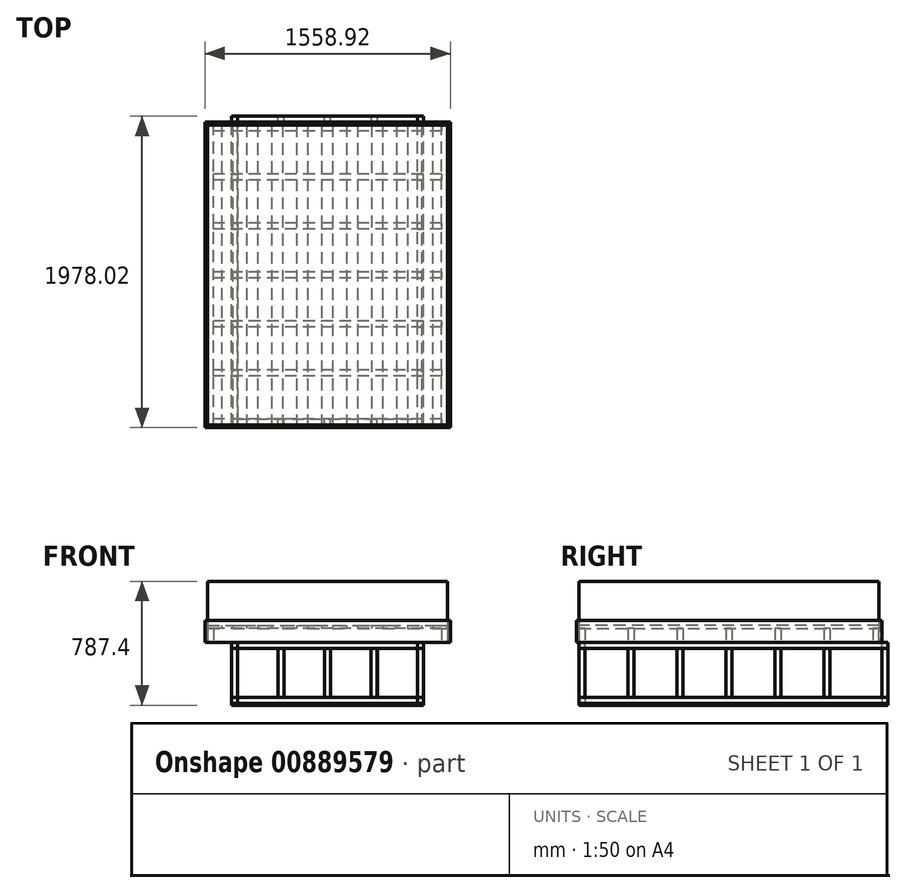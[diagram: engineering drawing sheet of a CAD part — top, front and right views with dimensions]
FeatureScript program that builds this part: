
annotation { "Feature Type Name" : "Feature", "Feature Type Description" : "" }
export const myFeature = defineFeature(function(context is Context, id is Id, definition is map)
    precondition{}
    {
        {
            var Q0;
            Q0=qCreatedBy(makeId("Top.planeOp"),FACE);
            var sketch = newSketch(context, id + "F0", { "sketchPlane" : qUnion([Q0])});
            skLineSegment(sketch, "E0.bottom", {"start": v(0, 0) * mm, "end": v(1524, 0) * mm});
            skLineSegment(sketch, "E0.top", {"start": v(0, -1905) * mm, "end": v(1524, -1905) * mm});
            skLineSegment(sketch, "E0.left", {"start": v(0, 0) * mm, "end": v(0, -1905) * mm});
            skLineSegment(sketch, "E0.right", {"start": v(1524, 0) * mm, "end": v(1524, -1905) * mm});
            skSolve(sketch);
        }
        {
            var Q0;
            Q0=makeQuery(id+"F0.imprint","IMPRINT",FACE,{"disambiguationData":[TD([[makeQuery(id+"F0.imprint","IMPRINT",EDGE,{"derivedFrom":sQuery(id+"F0.wireOp",EDGE,"E0.bottom")}),-1.0]])]});
            extrude(context, id + "F1", {"entities" : qUnion([Q0]), "depth" : 787.4 * mm, "offsetDistance" : 25.4 * mm, "hasSecondDirection" : true, "secondDirectionOppositeDirection" : true, "secondDirectionDepth" : -508 * mm});
        }
        {
            var Q0;
            Q0=makeQuery(id+"F1.opExtrude","SWEPT_FACE",FACE,{"disambiguationData":[OSD([sQuery(id+"F0.wireOp",EDGE,"E0.top")])]});
            var sketch = newSketch(context, id + "F2", { "sketchPlane" : qUnion([Q0])});
            skLineSegment(sketch, "E1.bottom", {"start": v(0, 508) * mm, "end": v(88.9, 508) * mm});
            skLineSegment(sketch, "E1.top", {"start": v(0, 488.95) * mm, "end": v(88.9, 488.95) * mm});
            skLineSegment(sketch, "E1.left", {"start": v(0, 508) * mm, "end": v(0, 488.95) * mm});
            skLineSegment(sketch, "E1.right", {"start": v(88.9, 508) * mm, "end": v(88.9, 488.95) * mm});
            skLineSegment(sketch, "E2.1.0.0", {"start": v(158.75, 508) * mm, "end": v(247.65, 508) * mm});
            skLineSegment(sketch, "E2.1.0.1", {"start": v(158.75, 508) * mm, "end": v(158.75, 488.95) * mm});
            skLineSegment(sketch, "E2.1.0.2", {"start": v(158.75, 488.95) * mm, "end": v(247.65, 488.95) * mm});
            skLineSegment(sketch, "E2.1.0.3", {"start": v(247.65, 508) * mm, "end": v(247.65, 488.95) * mm});
            skLineSegment(sketch, "E2.2.0.0", {"start": v(317.5, 508) * mm, "end": v(406.4, 508) * mm});
            skLineSegment(sketch, "E2.2.0.1", {"start": v(317.5, 508) * mm, "end": v(317.5, 488.95) * mm});
            skLineSegment(sketch, "E2.2.0.2", {"start": v(317.5, 488.95) * mm, "end": v(406.4, 488.95) * mm});
            skLineSegment(sketch, "E2.2.0.3", {"start": v(406.4, 508) * mm, "end": v(406.4, 488.95) * mm});
            skLineSegment(sketch, "E2.3.0.0", {"start": v(476.25, 508) * mm, "end": v(565.15, 508) * mm});
            skLineSegment(sketch, "E2.3.0.1", {"start": v(476.25, 508) * mm, "end": v(476.25, 488.95) * mm});
            skLineSegment(sketch, "E2.3.0.2", {"start": v(476.25, 488.95) * mm, "end": v(565.15, 488.95) * mm});
            skLineSegment(sketch, "E2.3.0.3", {"start": v(565.15, 508) * mm, "end": v(565.15, 488.95) * mm});
            skLineSegment(sketch, "E2.4.0.0", {"start": v(635, 508) * mm, "end": v(723.9, 508) * mm});
            skLineSegment(sketch, "E2.4.0.1", {"start": v(635, 508) * mm, "end": v(635, 488.95) * mm});
            skLineSegment(sketch, "E2.4.0.2", {"start": v(635, 488.95) * mm, "end": v(723.9, 488.95) * mm});
            skLineSegment(sketch, "E2.4.0.3", {"start": v(723.9, 508) * mm, "end": v(723.9, 488.95) * mm});
            skLineSegment(sketch, "E2.5.0.0", {"start": v(793.75, 508) * mm, "end": v(882.65, 508) * mm});
            skLineSegment(sketch, "E2.5.0.1", {"start": v(793.75, 508) * mm, "end": v(793.75, 488.95) * mm});
            skLineSegment(sketch, "E2.5.0.2", {"start": v(793.75, 488.95) * mm, "end": v(882.65, 488.95) * mm});
            skLineSegment(sketch, "E2.5.0.3", {"start": v(882.65, 508) * mm, "end": v(882.65, 488.95) * mm});
            skLineSegment(sketch, "E2.6.0.0", {"start": v(952.5, 508) * mm, "end": v(1041.4, 508) * mm});
            skLineSegment(sketch, "E2.6.0.1", {"start": v(952.5, 508) * mm, "end": v(952.5, 488.95) * mm});
            skLineSegment(sketch, "E2.6.0.2", {"start": v(952.5, 488.95) * mm, "end": v(1041.4, 488.95) * mm});
            skLineSegment(sketch, "E2.6.0.3", {"start": v(1041.4, 508) * mm, "end": v(1041.4, 488.95) * mm});
            skLineSegment(sketch, "E2.7.0.0", {"start": v(1111.25, 508) * mm, "end": v(1200.15, 508) * mm});
            skLineSegment(sketch, "E2.7.0.1", {"start": v(1111.25, 508) * mm, "end": v(1111.25, 488.95) * mm});
            skLineSegment(sketch, "E2.7.0.2", {"start": v(1111.25, 488.95) * mm, "end": v(1200.15, 488.95) * mm});
            skLineSegment(sketch, "E2.7.0.3", {"start": v(1200.15, 508) * mm, "end": v(1200.15, 488.95) * mm});
            skLineSegment(sketch, "E2.8.0.0", {"start": v(1270, 508) * mm, "end": v(1358.9, 508) * mm});
            skLineSegment(sketch, "E2.8.0.1", {"start": v(1270, 508) * mm, "end": v(1270, 488.95) * mm});
            skLineSegment(sketch, "E2.8.0.2", {"start": v(1270, 488.95) * mm, "end": v(1358.9, 488.95) * mm});
            skLineSegment(sketch, "E2.8.0.3", {"start": v(1358.9, 508) * mm, "end": v(1358.9, 488.95) * mm});
            skLineSegment(sketch, "E2.9.0.0", {"start": v(1428.75, 508) * mm, "end": v(1517.65, 508) * mm});
            skLineSegment(sketch, "E2.9.0.1", {"start": v(1428.75, 508) * mm, "end": v(1428.75, 488.95) * mm});
            skLineSegment(sketch, "E2.9.0.2", {"start": v(1428.75, 488.95) * mm, "end": v(1517.65, 488.95) * mm});
            skLineSegment(sketch, "E2.9.0.3", {"start": v(1517.65, 508) * mm, "end": v(1517.65, 488.95) * mm});
            skLineSegment(sketch, "E2.direction1", {"start": v(0, 508) * mm, "end": v(158.75, 508) * mm, "construction": true});
            skSolve(sketch);
        }
        {
            var Q0;
            Q0 = qSketchRegion(id + "F2", true);
            var Q1;
            Q1=makeQuery(id+"F1.opExtrude","SWEPT_FACE",FACE,{"disambiguationData":[OSD([sQuery(id+"F0.wireOp",EDGE,"E0.bottom")])]});
            extrude(context, id + "F3", {"entities" : qUnion([Q0]), "endBound" : BoundingType.UP_TO_SURFACE, "oppositeDirection" : true, "depth" : 25.4 * mm, "endBoundEntityFace" : qUnion([Q1]), "offsetDistance" : 25.4 * mm});
        }
        {
            var Q0;
            Q0=makeQuery(id+"F1.opExtrude","SWEPT_FACE",FACE,{"disambiguationData":[OSD([sQuery(id+"F0.wireOp",EDGE,"E0.bottom")])]});
            var sketch = newSketch(context, id + "F4", { "sketchPlane" : qUnion([Q0])});
            skLineSegment(sketch, "E3.bottom", {"start": v(-1524, 400.05) * mm, "end": v(-1485.9, 400.05) * mm});
            skLineSegment(sketch, "E3.top", {"start": v(-1524, 488.95) * mm, "end": v(-1485.9, 488.95) * mm});
            skLineSegment(sketch, "E3.left", {"start": v(-1524, 400.05) * mm, "end": v(-1524, 488.95) * mm});
            skLineSegment(sketch, "E3.right", {"start": v(-1485.9, 400.05) * mm, "end": v(-1485.9, 488.95) * mm});
            skLineSegment(sketch, "E4.bottom", {"start": v(0, 400.05) * mm, "end": v(-38.1, 400.05) * mm});
            skLineSegment(sketch, "E4.top", {"start": v(0, 488.95) * mm, "end": v(-38.1, 488.95) * mm});
            skLineSegment(sketch, "E4.left", {"start": v(0, 400.05) * mm, "end": v(0, 488.95) * mm});
            skLineSegment(sketch, "E4.right", {"start": v(-38.1, 400.05) * mm, "end": v(-38.1, 488.95) * mm});
            skSolve(sketch);
        }
        {
            var Q0;
            Q0 = qSketchRegion(id + "F4", true);
            var Q1;
            Q1=makeQuery(id+"F1.opExtrude","SWEPT_FACE",FACE,{"disambiguationData":[OSD([sQuery(id+"F0.wireOp",EDGE,"E0.top")])]});
            extrude(context, id + "F5", {"entities" : qUnion([Q0]), "endBound" : BoundingType.UP_TO_SURFACE, "oppositeDirection" : true, "depth" : 25.4 * mm, "endBoundEntityFace" : qUnion([Q1]), "offsetDistance" : 25.4 * mm});
        }
        {
            var Q0;
            Q0=makeQuery(id+"F5.opExtrude","SWEPT_FACE",FACE,{"disambiguationData":[OSD([sQuery(id+"F4.wireOp",EDGE,"E4.right")])]});
            var sketch = newSketch(context, id + "F6", { "sketchPlane" : qUnion([Q0])});
            skLineSegment(sketch, "E5.bottom", {"start": v(0, 400.05) * mm, "end": v(-38.1, 400.05) * mm});
            skLineSegment(sketch, "E5.top", {"start": v(0, 488.95) * mm, "end": v(-38.1, 488.95) * mm});
            skLineSegment(sketch, "E5.left", {"start": v(0, 400.05) * mm, "end": v(0, 488.95) * mm});
            skLineSegment(sketch, "E5.right", {"start": v(-38.1, 400.05) * mm, "end": v(-38.1, 488.95) * mm});
            skLineSegment(sketch, "E6.1.0.0", {"start": v(-311.15, 400.05) * mm, "end": v(-349.25, 400.05) * mm});
            skLineSegment(sketch, "E6.1.0.1", {"start": v(-311.15, 488.95) * mm, "end": v(-349.25, 488.95) * mm});
            skLineSegment(sketch, "E6.1.0.2", {"start": v(-311.15, 400.05) * mm, "end": v(-311.15, 488.95) * mm});
            skLineSegment(sketch, "E6.1.0.3", {"start": v(-349.25, 400.05) * mm, "end": v(-349.25, 488.95) * mm});
            skLineSegment(sketch, "E6.2.0.0", {"start": v(-622.3, 400.05) * mm, "end": v(-660.4, 400.05) * mm});
            skLineSegment(sketch, "E6.2.0.1", {"start": v(-622.3, 488.95) * mm, "end": v(-660.4, 488.95) * mm});
            skLineSegment(sketch, "E6.2.0.2", {"start": v(-622.3, 400.05) * mm, "end": v(-622.3, 488.95) * mm});
            skLineSegment(sketch, "E6.2.0.3", {"start": v(-660.4, 400.05) * mm, "end": v(-660.4, 488.95) * mm});
            skLineSegment(sketch, "E6.3.0.0", {"start": v(-933.45, 400.05) * mm, "end": v(-971.55, 400.05) * mm});
            skLineSegment(sketch, "E6.3.0.1", {"start": v(-933.45, 488.95) * mm, "end": v(-971.55, 488.95) * mm});
            skLineSegment(sketch, "E6.3.0.2", {"start": v(-933.45, 400.05) * mm, "end": v(-933.45, 488.95) * mm});
            skLineSegment(sketch, "E6.3.0.3", {"start": v(-971.55, 400.05) * mm, "end": v(-971.55, 488.95) * mm});
            skLineSegment(sketch, "E6.4.0.0", {"start": v(-1244.6, 400.05) * mm, "end": v(-1282.7, 400.05) * mm});
            skLineSegment(sketch, "E6.4.0.1", {"start": v(-1244.6, 488.95) * mm, "end": v(-1282.7, 488.95) * mm});
            skLineSegment(sketch, "E6.4.0.2", {"start": v(-1244.6, 400.05) * mm, "end": v(-1244.6, 488.95) * mm});
            skLineSegment(sketch, "E6.4.0.3", {"start": v(-1282.7, 400.05) * mm, "end": v(-1282.7, 488.95) * mm});
            skLineSegment(sketch, "E6.5.0.0", {"start": v(-1555.75, 400.05) * mm, "end": v(-1593.85, 400.05) * mm});
            skLineSegment(sketch, "E6.5.0.1", {"start": v(-1555.75, 488.95) * mm, "end": v(-1593.85, 488.95) * mm});
            skLineSegment(sketch, "E6.5.0.2", {"start": v(-1555.75, 400.05) * mm, "end": v(-1555.75, 488.95) * mm});
            skLineSegment(sketch, "E6.5.0.3", {"start": v(-1593.85, 400.05) * mm, "end": v(-1593.85, 488.95) * mm});
            skLineSegment(sketch, "E6.6.0.0", {"start": v(-1866.9, 400.05) * mm, "end": v(-1905, 400.05) * mm});
            skLineSegment(sketch, "E6.6.0.1", {"start": v(-1866.9, 488.95) * mm, "end": v(-1905, 488.95) * mm});
            skLineSegment(sketch, "E6.6.0.2", {"start": v(-1866.9, 400.05) * mm, "end": v(-1866.9, 488.95) * mm});
            skLineSegment(sketch, "E6.6.0.3", {"start": v(-1905, 400.05) * mm, "end": v(-1905, 488.95) * mm});
            skLineSegment(sketch, "E6.direction1", {"start": v(-38.1, 400.05) * mm, "end": v(-349.25, 400.05) * mm, "construction": true});
            skSolve(sketch);
        }
        {
            var Q0;
            Q0 = qSketchRegion(id + "F6", true);
            var Q1;
            Q1=makeQuery(id+"F5.opExtrude","SWEPT_FACE",FACE,{"disambiguationData":[OSD([sQuery(id+"F4.wireOp",EDGE,"E3.right")])]});
            extrude(context, id + "F7", {"entities" : qUnion([Q0]), "endBound" : BoundingType.UP_TO_SURFACE, "depth" : 25.4 * mm, "endBoundEntityFace" : qUnion([Q1]), "offsetDistance" : 25.4 * mm});
        }
        {
            var Q0;
            Q0=makeQuery(id+"F5.opExtrude","SWEPT_FACE",FACE,{"disambiguationData":[OSD([sQuery(id+"F4.wireOp",EDGE,"E4.bottom")])]});
            var sketch = newSketch(context, id + "F8", { "sketchPlane" : qUnion([Q0])});
            skLineSegment(sketch, "E7.left", {"start": v(1541.46, -17.46) * mm, "end": v(1541.46, 1922.46) * mm});
            skLineSegment(sketch, "E7.right", {"start": v(-17.46, -17.46) * mm, "end": v(-17.46, 1922.46) * mm});
            skLineSegment(sketch, "E8.left", {"start": v(1524, 0) * mm, "end": v(1524, 1905) * mm});
            skLineSegment(sketch, "E8.right", {"start": v(0, 0) * mm, "end": v(0, 1905) * mm});
            skLineSegment(sketch, "E9", {"start": v(0, 1905) * mm, "end": v(-17.46, 1922.46) * mm});
            skLineSegment(sketch, "E10", {"start": v(1524, 1905) * mm, "end": v(1541.46, 1922.46) * mm});
            skLineSegment(sketch, "E11", {"start": v(1524, 0) * mm, "end": v(1541.46, -17.46) * mm});
            skLineSegment(sketch, "E12", {"start": v(0, 0) * mm, "end": v(-17.46, -17.46) * mm});
            skSolve(sketch);
        }
        {
            var Q0;
            Q0=makeQuery(id+"F7.opExtrude","SWEPT_FACE",FACE,{"disambiguationData":[OSD([sQuery(id+"F6.wireOp",EDGE,"E5.bottom")])]});
            var sketch = newSketch(context, id + "F9", { "sketchPlane" : qUnion([Q0])});
            skLineSegment(sketch, "E13.0", {"start": v(1524, 0) * mm, "end": v(1541.46, -17.46) * mm});
            skLineSegment(sketch, "E14.0", {"start": v(0, 0) * mm, "end": v(-17.46, -17.46) * mm});
            skLineSegment(sketch, "E15", {"start": v(0, 0) * mm, "end": v(1524, 0) * mm});
            skLineSegment(sketch, "E16", {"start": v(1541.46, -17.46) * mm, "end": v(-17.46, -17.46) * mm});
            skLineSegment(sketch, "E17.0", {"start": v(0, 1905) * mm, "end": v(-17.46, 1922.46) * mm});
            skLineSegment(sketch, "E18.0", {"start": v(1524, 1905) * mm, "end": v(1541.46, 1922.46) * mm});
            skLineSegment(sketch, "E19", {"start": v(1524, 1905) * mm, "end": v(0, 1905) * mm});
            skLineSegment(sketch, "E20", {"start": v(-17.46, 1922.46) * mm, "end": v(1541.46, 1922.46) * mm});
            skSolve(sketch);
        }
        {
            var Q0;
            Q0 = qSketchRegion(id + "F8", true);
            var Q1;
            Q1 = qSketchRegion(id + "F9", true);
            extrude(context, id + "F10", {"entities" : qUnion([Q0, Q1]), "oppositeDirection" : true, "depth" : 139.7 * mm, "offsetDistance" : 25.4 * mm});
        }
        {
            var Q0;
            Q0=makeQuery(id+"F7.opExtrude","SWEPT_FACE",FACE,{"disambiguationData":[OSD([sQuery(id+"F6.wireOp",EDGE,"E6.5.0.0")])]});
            var sketch = newSketch(context, id + "F11", { "sketchPlane" : qUnion([Q0])});
            skLineSegment(sketch, "E21.bottom", {"start": v(152.41, 1905) * mm, "end": v(190.51, 1905) * mm});
            skLineSegment(sketch, "E21.top", {"start": v(152.41, -55.56) * mm, "end": v(190.51, -55.56) * mm});
            skLineSegment(sketch, "E21.left", {"start": v(152.41, 1905) * mm, "end": v(152.41, -55.56) * mm});
            skLineSegment(sketch, "E21.right", {"start": v(190.51, 1905) * mm, "end": v(190.51, -55.56) * mm});
            skLineSegment(sketch, "E22.bottom", {"start": v(1333.49, 1905) * mm, "end": v(1371.59, 1905) * mm});
            skLineSegment(sketch, "E22.top", {"start": v(1333.49, -55.56) * mm, "end": v(1371.59, -55.56) * mm});
            skLineSegment(sketch, "E22.left", {"start": v(1333.49, 1905) * mm, "end": v(1333.49, -55.56) * mm});
            skLineSegment(sketch, "E22.right", {"start": v(1371.59, 1905) * mm, "end": v(1371.59, -55.56) * mm});
            skSolve(sketch);
        }
        {
            var Q0;
            Q0=makeQuery(id+"F7.opExtrude","SWEPT_FACE",FACE,{"disambiguationData":[OSD([sQuery(id+"F6.wireOp",EDGE,"E6.1.0.0")])]});
            var sketch = newSketch(context, id + "F12", { "sketchPlane" : qUnion([Q0])});
            skLineSegment(sketch, "E23.bottom", {"start": v(190.51, 1905) * mm, "end": v(1333.49, 1905) * mm});
            skLineSegment(sketch, "E23.top", {"start": v(190.51, 1866.9) * mm, "end": v(1333.49, 1866.9) * mm});
            skLineSegment(sketch, "E23.left", {"start": v(190.51, 1905) * mm, "end": v(190.51, 1866.9) * mm});
            skLineSegment(sketch, "E23.right", {"start": v(1333.49, 1905) * mm, "end": v(1333.49, 1866.9) * mm});
            skLineSegment(sketch, "E24.bottom", {"start": v(190.51, -17.46) * mm, "end": v(1333.49, -17.46) * mm});
            skLineSegment(sketch, "E24.top", {"start": v(190.51, -55.56) * mm, "end": v(1333.49, -55.56) * mm});
            skLineSegment(sketch, "E24.left", {"start": v(190.51, -17.46) * mm, "end": v(190.51, -55.56) * mm});
            skLineSegment(sketch, "E24.right", {"start": v(1333.49, -17.46) * mm, "end": v(1333.49, -55.56) * mm});
            skSolve(sketch);
        }
        {
            var Q0;
            Q0 = qSketchRegion(id + "F11", true);
            var Q1;
            Q1 = qSketchRegion(id + "F12", true);
            extrude(context, id + "F13", {"entities" : qUnion([Q0, Q1]), "depth" : 38.1 * mm, "offsetDistance" : 25.4 * mm});
        }
        {
            var Q0;
            Q0=qCreatedBy(makeId("Top.planeOp"),FACE);
            var sketch = newSketch(context, id + "F14", { "sketchPlane" : qUnion([Q0])});
            skLineSegment(sketch, "E25.0", {"start": v(152.41, -1905) * mm, "end": v(152.41, 55.56) * mm});
            skLineSegment(sketch, "E26.0", {"start": v(152.41, 55.56) * mm, "end": v(1371.59, 55.56) * mm});
            skLineSegment(sketch, "E27.0", {"start": v(152.41, -1905) * mm, "end": v(1371.59, -1905) * mm});
            skLineSegment(sketch, "E28.0", {"start": v(1371.59, -1905) * mm, "end": v(1371.59, 55.56) * mm});
            skPoint(sketch, "E29.orphan", {"position": v(1333.49, 55.56) * mm});
            skPoint(sketch, "E30.orphan", {"position": v(1333.49, -1905) * mm});
            skPoint(sketch, "E31.orphan", {"position": v(190.51, -1905) * mm});
            skPoint(sketch, "E32.orphan", {"position": v(190.51, 55.56) * mm});
            skSolve(sketch);
        }
        {
            var Q0;
            Q0 = qSketchRegion(id + "F14", true);
            extrude(context, id + "F15", {"entities" : qUnion([Q0]), "depth" : 12.7 * mm, "offsetDistance" : 25.4 * mm});
        }
        {
            var Q0;
            Q0=makeQuery(id+"F15.opExtrude","CAP_FACE",FACE,{"disambiguationData":[OSD([sQuery(id+"F14.wireOp",EDGE,"E25.0"),sQuery(id+"F14.wireOp",EDGE,"E26.0"),sQuery(id+"F14.wireOp",EDGE,"E27.0"),sQuery(id+"F14.wireOp",EDGE,"E28.0")])],"isStart":false});
            var sketch = newSketch(context, id + "F16", { "sketchPlane" : qUnion([Q0])});
            skLineSegment(sketch, "E33.0.0", {"start": v(1371.59, 55.56) * mm, "end": v(1371.59, -1905) * mm});
            skLineSegment(sketch, "E33.0.1", {"start": v(1371.59, -1905) * mm, "end": v(1333.49, -1905) * mm});
            skLineSegment(sketch, "E33.0.2", {"start": v(1333.49, -1905) * mm, "end": v(1333.49, 55.56) * mm});
            skLineSegment(sketch, "E33.0.3", {"start": v(1333.49, 55.56) * mm, "end": v(1371.59, 55.56) * mm});
            skLineSegment(sketch, "E34.0.0", {"start": v(152.41, 55.56) * mm, "end": v(190.51, 55.56) * mm});
            skLineSegment(sketch, "E34.0.1", {"start": v(190.51, 55.56) * mm, "end": v(190.51, -1905) * mm});
            skLineSegment(sketch, "E34.0.2", {"start": v(190.51, -1905) * mm, "end": v(152.41, -1905) * mm});
            skLineSegment(sketch, "E34.0.3", {"start": v(152.41, -1905) * mm, "end": v(152.41, 55.56) * mm});
            skSolve(sketch);
        }
        {
            var Q0;
            {var subQ0=sQuery(id+"F16.wireOp",EDGE,"E33.0.2");Q0=makeQuery(id+"F16.imprint","IMPRINT",FACE,{"disambiguationData":[TD([[makeQuery(id+"F16.imprint","IMPRINT",EDGE,{"derivedFrom":subQ0}),1.0]])]});}
            var sketch = newSketch(context, id + "F17", { "sketchPlane" : qUnion([Q0])});
            skLineSegment(sketch, "E35.0.0", {"start": v(190.51, -1905) * mm, "end": v(190.51, -1866.9) * mm});
            skLineSegment(sketch, "E35.0.1", {"start": v(190.51, -1866.9) * mm, "end": v(1333.49, -1866.9) * mm});
            skLineSegment(sketch, "E35.0.2", {"start": v(1333.49, -1866.9) * mm, "end": v(1333.49, -1905) * mm});
            skLineSegment(sketch, "E35.0.3", {"start": v(1333.49, -1905) * mm, "end": v(190.51, -1905) * mm});
            skLineSegment(sketch, "E36.0.0", {"start": v(190.51, 17.46) * mm, "end": v(190.51, 55.56) * mm});
            skLineSegment(sketch, "E36.0.1", {"start": v(190.51, 55.56) * mm, "end": v(1333.49, 55.56) * mm});
            skLineSegment(sketch, "E36.0.2", {"start": v(1333.49, 55.56) * mm, "end": v(1333.49, 17.46) * mm});
            skLineSegment(sketch, "E36.0.3", {"start": v(1333.49, 17.46) * mm, "end": v(190.51, 17.46) * mm});
            skSolve(sketch);
        }
        {
            var Q0;
            Q0 = qSketchRegion(id + "F16", true);
            var Q1;
            Q1 = qSketchRegion(id + "F17", true);
            extrude(context, id + "F18", {"entities" : qUnion([Q0, Q1]), "depth" : 38.1 * mm, "offsetDistance" : 25.4 * mm});
        }
        {
            var Q0;
            Q0=makeQuery(id+"F13.opExtrude","CAP_FACE",FACE,{"disambiguationData":[OSD([sQuery(id+"F11.wireOp",EDGE,"E21.bottom"),sQuery(id+"F11.wireOp",EDGE,"E21.top"),sQuery(id+"F11.wireOp",EDGE,"E21.left"),sQuery(id+"F11.wireOp",EDGE,"E21.right")])],"isStart":false});
            var sketch = newSketch(context, id + "F19", { "sketchPlane" : qUnion([Q0])});
            skLineSegment(sketch, "E37.bottom", {"start": v(152.41, 1866.9) * mm, "end": v(190.51, 1866.9) * mm});
            skLineSegment(sketch, "E37.top", {"start": v(152.41, 1905) * mm, "end": v(190.51, 1905) * mm});
            skLineSegment(sketch, "E37.left", {"start": v(152.41, 1866.9) * mm, "end": v(152.41, 1905) * mm});
            skLineSegment(sketch, "E37.right", {"start": v(190.51, 1866.9) * mm, "end": v(190.51, 1905) * mm});
            skLineSegment(sketch, "E38.bottom", {"start": v(190.51, 1555.75) * mm, "end": v(152.41, 1555.75) * mm});
            skLineSegment(sketch, "E38.top", {"start": v(190.51, 1593.85) * mm, "end": v(152.41, 1593.85) * mm});
            skLineSegment(sketch, "E38.left", {"start": v(190.51, 1555.75) * mm, "end": v(190.51, 1593.85) * mm});
            skLineSegment(sketch, "E38.right", {"start": v(152.41, 1555.75) * mm, "end": v(152.41, 1593.85) * mm});
            skLineSegment(sketch, "E39.0.1.0", {"start": v(190.51, 1244.6) * mm, "end": v(152.41, 1244.6) * mm});
            skLineSegment(sketch, "E39.0.1.1", {"start": v(190.51, 1244.6) * mm, "end": v(190.51, 1282.7) * mm});
            skLineSegment(sketch, "E39.0.1.2", {"start": v(190.51, 1282.7) * mm, "end": v(152.41, 1282.7) * mm});
            skLineSegment(sketch, "E39.0.1.3", {"start": v(152.41, 1244.6) * mm, "end": v(152.41, 1282.7) * mm});
            skLineSegment(sketch, "E39.0.2.0", {"start": v(190.51, 933.45) * mm, "end": v(152.41, 933.45) * mm});
            skLineSegment(sketch, "E39.0.2.1", {"start": v(190.51, 933.45) * mm, "end": v(190.51, 971.55) * mm});
            skLineSegment(sketch, "E39.0.2.2", {"start": v(190.51, 971.55) * mm, "end": v(152.41, 971.55) * mm});
            skLineSegment(sketch, "E39.0.2.3", {"start": v(152.41, 933.45) * mm, "end": v(152.41, 971.55) * mm});
            skLineSegment(sketch, "E39.0.3.0", {"start": v(190.51, 622.3) * mm, "end": v(152.41, 622.3) * mm});
            skLineSegment(sketch, "E39.0.3.1", {"start": v(190.51, 622.3) * mm, "end": v(190.51, 660.4) * mm});
            skLineSegment(sketch, "E39.0.3.2", {"start": v(190.51, 660.4) * mm, "end": v(152.41, 660.4) * mm});
            skLineSegment(sketch, "E39.0.3.3", {"start": v(152.41, 622.3) * mm, "end": v(152.41, 660.4) * mm});
            skLineSegment(sketch, "E39.0.4.0", {"start": v(190.51, 311.15) * mm, "end": v(152.41, 311.15) * mm});
            skLineSegment(sketch, "E39.0.4.1", {"start": v(190.51, 311.15) * mm, "end": v(190.51, 349.25) * mm});
            skLineSegment(sketch, "E39.0.4.2", {"start": v(190.51, 349.25) * mm, "end": v(152.41, 349.25) * mm});
            skLineSegment(sketch, "E39.0.4.3", {"start": v(152.41, 311.15) * mm, "end": v(152.41, 349.25) * mm});
            skLineSegment(sketch, "E39.1.0.0", {"start": v(1371.61, 1555.75) * mm, "end": v(1333.51, 1555.75) * mm});
            skLineSegment(sketch, "E39.1.0.1", {"start": v(1371.61, 1555.75) * mm, "end": v(1371.61, 1593.85) * mm});
            skLineSegment(sketch, "E39.1.0.2", {"start": v(1371.61, 1593.85) * mm, "end": v(1333.51, 1593.85) * mm});
            skLineSegment(sketch, "E39.1.0.3", {"start": v(1333.51, 1555.75) * mm, "end": v(1333.51, 1593.85) * mm});
            skLineSegment(sketch, "E39.1.1.0", {"start": v(1371.61, 1244.6) * mm, "end": v(1333.51, 1244.6) * mm});
            skLineSegment(sketch, "E39.1.1.1", {"start": v(1371.61, 1244.6) * mm, "end": v(1371.61, 1282.7) * mm});
            skLineSegment(sketch, "E39.1.1.2", {"start": v(1371.61, 1282.7) * mm, "end": v(1333.51, 1282.7) * mm});
            skLineSegment(sketch, "E39.1.1.3", {"start": v(1333.51, 1244.6) * mm, "end": v(1333.51, 1282.7) * mm});
            skLineSegment(sketch, "E39.1.2.0", {"start": v(1371.61, 933.45) * mm, "end": v(1333.51, 933.45) * mm});
            skLineSegment(sketch, "E39.1.2.1", {"start": v(1371.61, 933.45) * mm, "end": v(1371.61, 971.55) * mm});
            skLineSegment(sketch, "E39.1.2.2", {"start": v(1371.61, 971.55) * mm, "end": v(1333.51, 971.55) * mm});
            skLineSegment(sketch, "E39.1.2.3", {"start": v(1333.51, 933.45) * mm, "end": v(1333.51, 971.55) * mm});
            skLineSegment(sketch, "E39.1.3.0", {"start": v(1371.61, 622.3) * mm, "end": v(1333.51, 622.3) * mm});
            skLineSegment(sketch, "E39.1.3.1", {"start": v(1371.61, 622.3) * mm, "end": v(1371.61, 660.4) * mm});
            skLineSegment(sketch, "E39.1.3.2", {"start": v(1371.61, 660.4) * mm, "end": v(1333.51, 660.4) * mm});
            skLineSegment(sketch, "E39.1.3.3", {"start": v(1333.51, 622.3) * mm, "end": v(1333.51, 660.4) * mm});
            skLineSegment(sketch, "E39.1.4.0", {"start": v(1371.61, 311.15) * mm, "end": v(1333.51, 311.15) * mm});
            skLineSegment(sketch, "E39.1.4.1", {"start": v(1371.61, 311.15) * mm, "end": v(1371.61, 349.25) * mm});
            skLineSegment(sketch, "E39.1.4.2", {"start": v(1371.61, 349.25) * mm, "end": v(1333.51, 349.25) * mm});
            skLineSegment(sketch, "E39.1.4.3", {"start": v(1333.51, 311.15) * mm, "end": v(1333.51, 349.25) * mm});
            skLineSegment(sketch, "E39.direction1", {"start": v(152.41, 1555.75) * mm, "end": v(1333.51, 1555.75) * mm, "construction": true});
            skLineSegment(sketch, "E39.direction2", {"start": v(152.41, 1555.75) * mm, "end": v(152.41, 1244.6) * mm, "construction": true});
            skLineSegment(sketch, "E40.1.0.0", {"start": v(447.69, 1866.9) * mm, "end": v(485.79, 1866.9) * mm});
            skLineSegment(sketch, "E40.1.0.1", {"start": v(447.69, 1866.9) * mm, "end": v(447.69, 1905) * mm});
            skLineSegment(sketch, "E40.1.0.2", {"start": v(447.69, 1905) * mm, "end": v(485.79, 1905) * mm});
            skLineSegment(sketch, "E40.1.0.3", {"start": v(485.79, 1866.9) * mm, "end": v(485.79, 1905) * mm});
            skLineSegment(sketch, "E40.2.0.0", {"start": v(742.96, 1866.9) * mm, "end": v(781.06, 1866.9) * mm});
            skLineSegment(sketch, "E40.2.0.1", {"start": v(742.96, 1866.9) * mm, "end": v(742.96, 1905) * mm});
            skLineSegment(sketch, "E40.2.0.2", {"start": v(742.96, 1905) * mm, "end": v(781.06, 1905) * mm});
            skLineSegment(sketch, "E40.2.0.3", {"start": v(781.06, 1866.9) * mm, "end": v(781.06, 1905) * mm});
            skLineSegment(sketch, "E40.3.0.0", {"start": v(1038.24, 1866.9) * mm, "end": v(1076.34, 1866.9) * mm});
            skLineSegment(sketch, "E40.3.0.1", {"start": v(1038.24, 1866.9) * mm, "end": v(1038.24, 1905) * mm});
            skLineSegment(sketch, "E40.3.0.2", {"start": v(1038.24, 1905) * mm, "end": v(1076.34, 1905) * mm});
            skLineSegment(sketch, "E40.3.0.3", {"start": v(1076.34, 1866.9) * mm, "end": v(1076.34, 1905) * mm});
            skLineSegment(sketch, "E40.4.0.0", {"start": v(1333.51, 1866.9) * mm, "end": v(1371.61, 1866.9) * mm});
            skLineSegment(sketch, "E40.4.0.1", {"start": v(1333.51, 1866.9) * mm, "end": v(1333.51, 1905) * mm});
            skLineSegment(sketch, "E40.4.0.2", {"start": v(1333.51, 1905) * mm, "end": v(1371.61, 1905) * mm});
            skLineSegment(sketch, "E40.4.0.3", {"start": v(1371.61, 1866.9) * mm, "end": v(1371.61, 1905) * mm});
            skLineSegment(sketch, "E40.direction1", {"start": v(152.41, 1866.9) * mm, "end": v(447.69, 1866.9) * mm, "construction": true});
            skLineSegment(sketch, "E41.1.4.0", {"start": v(1371.59, -55.56) * mm, "end": v(1333.49, -55.56) * mm});
            skLineSegment(sketch, "E41.1.4.1", {"start": v(1371.59, -55.56) * mm, "end": v(1371.59, -17.46) * mm});
            skLineSegment(sketch, "E41.1.4.2", {"start": v(1371.59, -17.46) * mm, "end": v(1333.49, -17.46) * mm});
            skLineSegment(sketch, "E41.1.4.3", {"start": v(1333.49, -55.56) * mm, "end": v(1333.49, -17.46) * mm});
            skLineSegment(sketch, "E42.1.1.0", {"start": v(152.41, -55.56) * mm, "end": v(190.51, -55.56) * mm});
            skLineSegment(sketch, "E42.1.1.1", {"start": v(152.41, -55.56) * mm, "end": v(152.41, -17.46) * mm});
            skLineSegment(sketch, "E42.1.1.2", {"start": v(152.41, -17.46) * mm, "end": v(190.51, -17.46) * mm});
            skLineSegment(sketch, "E42.1.1.3", {"start": v(190.51, -55.56) * mm, "end": v(190.51, -17.46) * mm});
            skLineSegment(sketch, "E43.1.1.0", {"start": v(742.96, -55.56) * mm, "end": v(781.06, -55.56) * mm});
            skLineSegment(sketch, "E43.1.1.1", {"start": v(742.96, -55.56) * mm, "end": v(742.96, -17.46) * mm});
            skLineSegment(sketch, "E43.1.1.2", {"start": v(742.96, -17.46) * mm, "end": v(781.06, -17.46) * mm});
            skLineSegment(sketch, "E43.1.1.3", {"start": v(781.06, -55.56) * mm, "end": v(781.06, -17.46) * mm});
            skLineSegment(sketch, "E44.1.1.0", {"start": v(447.69, -55.56) * mm, "end": v(485.79, -55.56) * mm});
            skLineSegment(sketch, "E44.1.1.1", {"start": v(447.69, -55.56) * mm, "end": v(447.69, -17.46) * mm});
            skLineSegment(sketch, "E44.1.1.2", {"start": v(447.69, -17.46) * mm, "end": v(485.79, -17.46) * mm});
            skLineSegment(sketch, "E44.1.1.3", {"start": v(485.79, -55.56) * mm, "end": v(485.79, -17.46) * mm});
            skLineSegment(sketch, "E45.1.4.0", {"start": v(1079.51, -55.56) * mm, "end": v(1041.41, -55.56) * mm});
            skLineSegment(sketch, "E45.1.4.1", {"start": v(1079.51, -55.56) * mm, "end": v(1079.51, -17.46) * mm});
            skLineSegment(sketch, "E45.1.4.2", {"start": v(1079.51, -17.46) * mm, "end": v(1041.41, -17.46) * mm});
            skLineSegment(sketch, "E45.1.4.3", {"start": v(1041.41, -55.56) * mm, "end": v(1041.41, -17.46) * mm});
            skSolve(sketch);
        }
        {
            var Q0;
            Q0 = qSketchRegion(id + "F19", true);
            var Q1;
            Q1=makeQuery(id+"F18.opExtrude","CAP_FACE",FACE,{"disambiguationData":[OSD([sQuery(id+"F16.wireOp",EDGE,"E33.0.0"),sQuery(id+"F16.wireOp",EDGE,"E33.0.1"),sQuery(id+"F16.wireOp",EDGE,"E33.0.2"),sQuery(id+"F16.wireOp",EDGE,"E33.0.3")])],"isStart":false});
            extrude(context, id + "F20", {"entities" : qUnion([Q0]), "endBound" : BoundingType.UP_TO_SURFACE, "depth" : 25.4 * mm, "endBoundEntityFace" : qUnion([Q1]), "offsetDistance" : 25.4 * mm});
        }
    });
